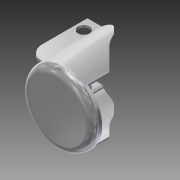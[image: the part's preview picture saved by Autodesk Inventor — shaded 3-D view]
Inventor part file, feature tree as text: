
AUTODESK INVENTOR PART (.ipt)
format: ipt  version: 2014 (Build 180170000, 170)  size: 285,696 bytes
history: native  units: mm
features: fillet x10, sketch x9, extrude x7, plane x5, chamfer x4, shell x1, hole x1
ambient origin geometry x8: Origin, YZ Plane, XZ Plane, XY Plane, X Axis, Y Axis, Z Axis, Center Point
bodies: Solid1 (feature_tree)
feature tree (37):
  extrude  "Extrusion1"  Depth=1.0mm TaperAngle=0.0deg
  shell  "Shell1"  Thickness=1.0mm
  sketch  "Sketch2"  dims[d4=29.0mm d5=30.0mm d8=26.0mm]
  plane  "Work Plane1"
  sketch  "Sketch4"  dims[d9=10.0mm d10=10.0mm]
  extrude  "Extrusion4"  Depth=30.0mm
  fillet  "Fillet1"  Radius=26.0mm
  extrude  "Extrusion5"  Depth=10.0mm
  chamfer  "Chamfer1"  Distance=25.0mm
  chamfer  "Chamfer2"  Distance=18.0mm
  chamfer  "Chamfer3"  Distance=9.0mm Angle=45.0deg
  fillet  "Fillet2"  Radius=9.0mm
  chamfer  "Chamfer4"  Distance=5.0mm Angle=45.0deg
  fillet  "Fillet3"  Radius=9.0mm
  fillet  "Fillet4"  Radius=4.0mm
  fillet  "Fillet5"  Radius=4.0mm
  fillet  "Fillet6"  Radius=15.0mm
  fillet  "Fillet7"  Radius=15.0mm
  plane  "Work Plane3"
  sketch  "Sketch6"  dims[d11=0.5mm]
  plane  "Work Plane4"
  plane  "Work Plane5"
  extrude  "Extrusion7"  Depth=1.0mm
  plane  "Work Plane6"
  extrude  "Extrusion8"  Depth=1.0mm TaperAngle=0.0deg
  extrude  "Extrusion9"  Depth=1.0mm
  extrude  "Extrusion10"  Depth=1.0mm
  fillet  "Fillet11"  Radius=25.0mm
  fillet  "Fillet12"  Radius=6.0mm
  fillet  "Fillet13"  Radius=1.0mm
  hole  "Hole3"  [1 undecoded]
  sketch  "Sketch1"  dims[d0=30.0mm d1=4.0mm d2=0.0mm d3=1.0mm]
  sketch  "Sketch9"  dims[d12=0.5mm d15=25.0mm d16=0.0mm]
  sketch  "Sketch10"  dims[d17=3.0mm d19=18.0mm d20=0.0mm d21=9.0mm d22=2.0mm d23=45.0deg]
  sketch  "Sketch11"  dims[d24=9.0mm d25=2.0mm d26=45.0deg]
  sketch  "Sketch12"  dims[d27=5.0mm d28=2.0mm d29=45.0deg d30=9.0mm d31=5.0mm d32=2.0mm d33=45.0deg d34=9.0mm d35=4.0mm d36=4.0mm d37=15.0mm d38=15.0mm]
  sketch  "Sketch13"  dims[d66=25.0mm d67=25.0mm d68=1.0mm d69=0.0mm d71=25.0mm d72=6.0mm d73=25.0mm d74=6.0mm d75=1.0mm d76=0.0mm d78=25.0mm d79=1.0mm d80=25.0mm d81=0.75mm d82=0.0mm d83=1.0mm d84=25.0mm d85=1.0mm d86=0.75mm d87=0.0mm d88=2.0mm d89=1.0mm d90=6.0mm d91=5.0mm d92=3.5mm d93=5.0mm d94=5.0mm d95=6.0mm d96=4.0mm d97=2.0mm d98=90.0deg d99=8.0mm d100=20.594885mm d44=1.0mm d45=1.0mm]
note: 1 required parameter value undecoded (feature->parameter linkage not recoverable at this tier; creation-order binding heuristic only, values carry confidence <= 0.55)
